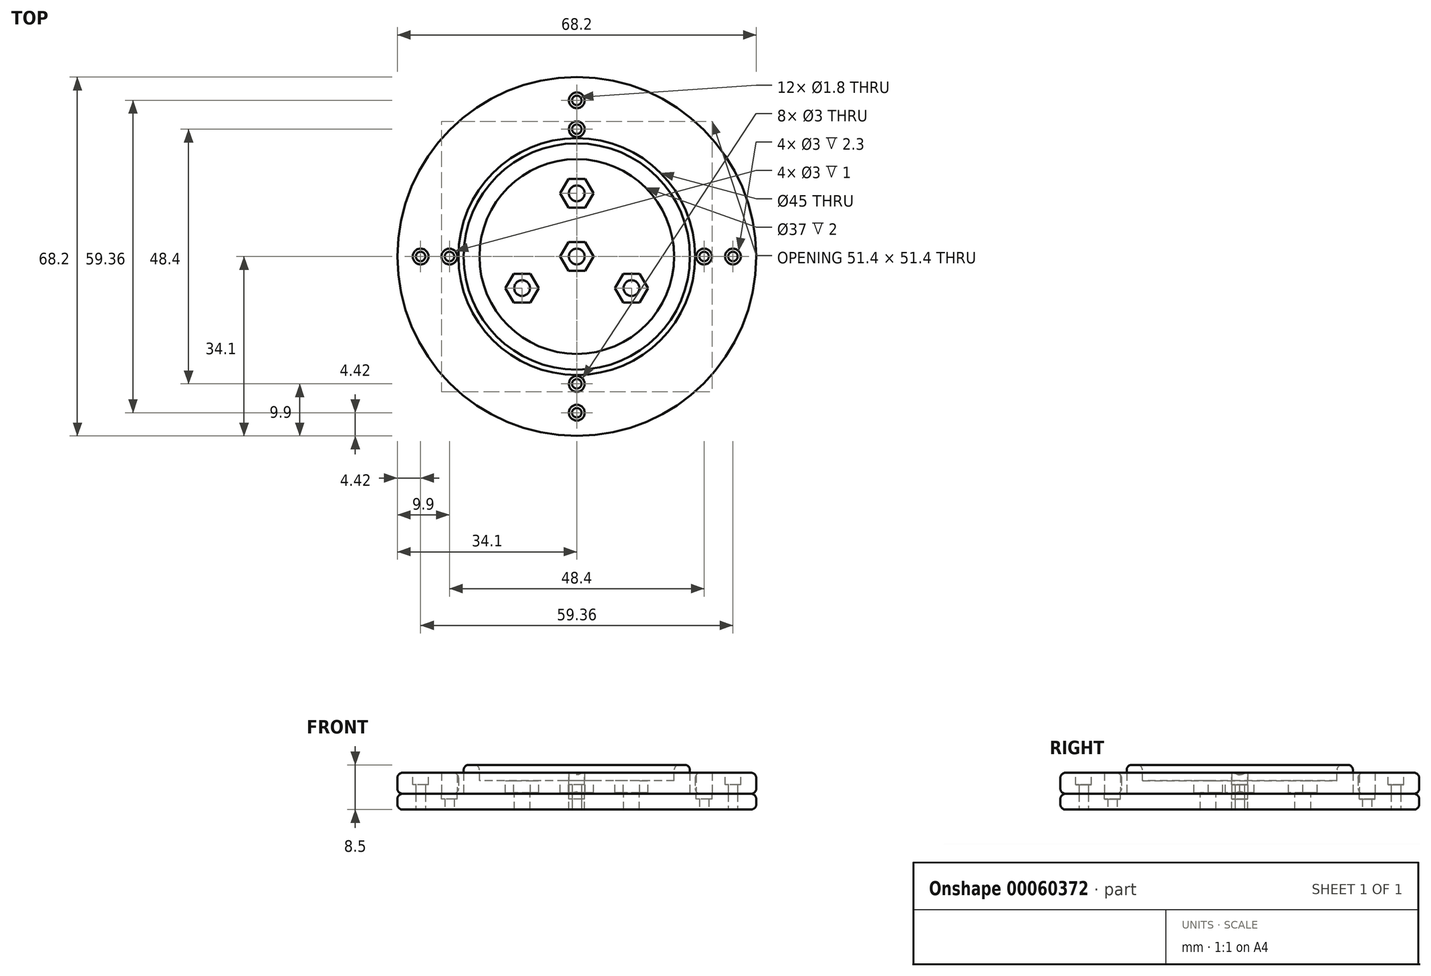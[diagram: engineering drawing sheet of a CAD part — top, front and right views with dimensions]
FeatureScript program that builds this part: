
annotation { "Feature Type Name" : "Feature", "Feature Type Description" : "" }
export const myFeature = defineFeature(function(context is Context, id is Id, definition is map)
    precondition{}
    {
        {
            var Q0;
            Q0=qCreatedBy(makeId("Top.planeOp"),FACE);
            var sketch = newSketch(context, id + "F0", { "sketchPlane" : qUnion([Q0])});
            skCircle(sketch, "E0", {"center": v(0, 0) * mm, "radius": 34.1 * mm});
            skCircle(sketch, "E1", {"center": v(0, 29.68) * mm, "radius": 0.9 * mm});
            skCircle(sketch, "E2", {"center": v(0, 24.2) * mm, "radius": 0.9 * mm});
            skCircle(sketch, "E3.1.0", {"center": v(-29.68, 0) * mm, "radius": 0.9 * mm});
            skCircle(sketch, "E3.1.1", {"center": v(-24.2, 0) * mm, "radius": 0.9 * mm});
            skCircle(sketch, "E3.2.0", {"center": v(0, -29.68) * mm, "radius": 0.9 * mm});
            skCircle(sketch, "E3.2.1", {"center": v(0, -24.2) * mm, "radius": 0.9 * mm});
            skCircle(sketch, "E3.3.0", {"center": v(29.68, 0) * mm, "radius": 0.9 * mm});
            skCircle(sketch, "E3.3.1", {"center": v(24.2, 0) * mm, "radius": 0.9 * mm});
            skSolve(sketch);
        }
        {
            var Q0;
            Q0=makeQuery(id+"F0.imprint","IMPRINT",FACE,{"disambiguationData":[TD([[makeQuery(id+"F0.imprint","IMPRINT",EDGE,{"derivedFrom":sQuery(id+"F0.wireOp",EDGE,"E0")}),1.0]])]});
            extrude(context, id + "F1", {"entities" : qUnion([Q0]), "depth" : 3 * mm});
        }
        {
            var Q0;
            Q0=makeQuery(id+"F1.opExtrude","CAP_FACE",FACE,{"disambiguationData":[OSD([sQuery(id+"F0.wireOp",EDGE,"E0"),sQuery(id+"F0.wireOp",EDGE,"E1"),sQuery(id+"F0.wireOp",EDGE,"E2"),sQuery(id+"F0.wireOp",EDGE,"E3.1.0"),sQuery(id+"F0.wireOp",EDGE,"E3.1.1"),sQuery(id+"F0.wireOp",EDGE,"E3.2.0"),sQuery(id+"F0.wireOp",EDGE,"E3.2.1"),sQuery(id+"F0.wireOp",EDGE,"E3.3.0"),sQuery(id+"F0.wireOp",EDGE,"E3.3.1")])],"isStart":false});
            var sketch = newSketch(context, id + "F2", { "sketchPlane" : qUnion([Q0])});
            skCircle(sketch, "E4", {"center": v(0, 24.2) * mm, "radius": 1.5 * mm});
            skCircle(sketch, "E5.1.0", {"center": v(-24.2, 0) * mm, "radius": 1.5 * mm});
            skCircle(sketch, "E5.2.0", {"center": v(0, -24.2) * mm, "radius": 1.5 * mm});
            skCircle(sketch, "E5.3.0", {"center": v(24.2, 0) * mm, "radius": 1.5 * mm});
            skPoint(sketch, "E5.center", {"position": v(0, 0) * mm});
            skSolve(sketch);
        }
        {
            var Q0;
            Q0 = qSketchRegion(id + "F2", true);
            extrude(context, id + "F3", {"entities" : qUnion([Q0]), "operationType" : NewBodyOperationType.REMOVE, "oppositeDirection" : true, "depth" : 1 * mm});
        }
        {
            var Q0;
            Q0=makeQuery(id+"F1.opExtrude","CAP_FACE",FACE,{"disambiguationData":[OSD([sQuery(id+"F0.wireOp",EDGE,"E0"),sQuery(id+"F0.wireOp",EDGE,"E1"),sQuery(id+"F0.wireOp",EDGE,"E2"),sQuery(id+"F0.wireOp",EDGE,"E3.1.0"),sQuery(id+"F0.wireOp",EDGE,"E3.1.1"),sQuery(id+"F0.wireOp",EDGE,"E3.2.0"),sQuery(id+"F0.wireOp",EDGE,"E3.2.1"),sQuery(id+"F0.wireOp",EDGE,"E3.3.0"),sQuery(id+"F0.wireOp",EDGE,"E3.3.1")])],"isStart":false});
            var sketch = newSketch(context, id + "F4", { "sketchPlane" : qUnion([Q0])});
            skCircle(sketch, "E6", {"center": v(0, 0) * mm, "radius": 21.5 * mm});
            skSolve(sketch);
        }
        {
            var Q0;
            Q0 = qSketchRegion(id + "F4", true);
            extrude(context, id + "F5", {"entities" : qUnion([Q0]), "operationType" : NewBodyOperationType.ADD, "depth" : 5.5 * mm});
        }
        {
            var Q0;
            Q0=makeQuery(id+"F5.opExtrude","CAP_FACE",FACE,{"disambiguationData":[OSD([sQuery(id+"F4.wireOp",EDGE,"E6")])],"isStart":false});
            var sketch = newSketch(context, id + "F6", { "sketchPlane" : qUnion([Q0])});
            skCircle(sketch, "E7", {"center": v(0, 0) * mm, "radius": 18.5 * mm});
            skSolve(sketch);
        }
        {
            var Q0;
            Q0 = qSketchRegion(id + "F6", true);
            extrude(context, id + "F7", {"entities" : qUnion([Q0]), "operationType" : NewBodyOperationType.REMOVE, "oppositeDirection" : true, "depth" : 3 * mm});
        }
        {
            var Q0;
            Q0=makeQuery(id+"F7.boolean.opBoolean","COPY",FACE,{"derivedFrom":makeQuery(id+"F7.opExtrude","CAP_FACE",FACE,{"disambiguationData":[OSD([sQuery(id+"F6.wireOp",EDGE,"E7")])],"isStart":false})});
            var sketch = newSketch(context, id + "F8", { "sketchPlane" : qUnion([Q0])});
            skCircle(sketch, "E8.cCircle", {"center": v(0, 12) * mm, "radius": 2.73 * mm, "construction": true});
            skLineSegment(sketch, "E8.0", {"start": v(1.58, 9.26) * mm, "end": v(-1.58, 9.26) * mm});
            skLineSegment(sketch, "E8.1", {"start": v(-1.58, 9.26) * mm, "end": v(-3.16, 12) * mm});
            skLineSegment(sketch, "E8.2", {"start": v(-3.16, 12) * mm, "end": v(-1.58, 14.73) * mm});
            skLineSegment(sketch, "E8.3", {"start": v(-1.58, 14.73) * mm, "end": v(1.58, 14.73) * mm});
            skLineSegment(sketch, "E8.4", {"start": v(1.58, 14.73) * mm, "end": v(3.16, 12) * mm});
            skLineSegment(sketch, "E8.5", {"start": v(3.16, 12) * mm, "end": v(1.58, 9.26) * mm});
            skPoint(sketch, "E8.0.midPoint", {"position": v(0, 9.27) * mm});
            skCircle(sketch, "E9", {"center": v(0, 12) * mm, "radius": 1.5 * mm});
            skPoint(sketch, "E10.1.0", {"position": v(-8.02, -4.63) * mm});
            skCircle(sketch, "E10.1.1", {"center": v(-10.4, -6) * mm, "radius": 1.5 * mm});
            skLineSegment(sketch, "E10.1.2", {"start": v(-11.97, -3.26) * mm, "end": v(-8.81, -3.26) * mm});
            skLineSegment(sketch, "E10.1.3", {"start": v(-13.55, -6) * mm, "end": v(-11.97, -3.26) * mm});
            skLineSegment(sketch, "E10.1.4", {"start": v(-11.97, -8.73) * mm, "end": v(-13.55, -6) * mm});
            skLineSegment(sketch, "E10.1.5", {"start": v(-8.81, -8.73) * mm, "end": v(-11.97, -8.73) * mm});
            skLineSegment(sketch, "E10.1.6", {"start": v(-7.23, -6) * mm, "end": v(-8.81, -8.73) * mm});
            skCircle(sketch, "E10.1.7", {"center": v(-10.4, -6) * mm, "radius": 2.73 * mm, "construction": true});
            skLineSegment(sketch, "E10.1.8", {"start": v(-8.81, -3.26) * mm, "end": v(-7.23, -6) * mm});
            skPoint(sketch, "E10.2.0", {"position": v(8.02, -4.63) * mm});
            skCircle(sketch, "E10.2.1", {"center": v(10.4, -6) * mm, "radius": 1.5 * mm});
            skLineSegment(sketch, "E10.2.2", {"start": v(8.81, -8.74) * mm, "end": v(7.23, -6) * mm});
            skLineSegment(sketch, "E10.2.3", {"start": v(11.97, -8.73) * mm, "end": v(8.81, -8.73) * mm});
            skLineSegment(sketch, "E10.2.4", {"start": v(13.55, -6) * mm, "end": v(11.97, -8.73) * mm});
            skLineSegment(sketch, "E10.2.5", {"start": v(11.97, -3.26) * mm, "end": v(13.55, -6) * mm});
            skLineSegment(sketch, "E10.2.6", {"start": v(8.81, -3.26) * mm, "end": v(11.97, -3.26) * mm});
            skCircle(sketch, "E10.2.7", {"center": v(10.4, -6) * mm, "radius": 2.73 * mm, "construction": true});
            skLineSegment(sketch, "E10.2.8", {"start": v(7.23, -6) * mm, "end": v(8.81, -3.26) * mm});
            skPoint(sketch, "E10.center", {"position": v(0, 0) * mm});
            skCircle(sketch, "E11", {"center": v(0, 0) * mm, "radius": 1.5 * mm});
            skCircle(sketch, "E12.cCircle", {"center": v(0, 0) * mm, "radius": 2.73 * mm, "construction": true});
            skLineSegment(sketch, "E12.0", {"start": v(1.58, -2.73) * mm, "end": v(-1.58, -2.73) * mm});
            skLineSegment(sketch, "E12.1", {"start": v(-1.58, -2.73) * mm, "end": v(-3.16, 0) * mm});
            skLineSegment(sketch, "E12.2", {"start": v(-3.16, 0) * mm, "end": v(-1.58, 2.73) * mm});
            skLineSegment(sketch, "E12.3", {"start": v(-1.58, 2.73) * mm, "end": v(1.58, 2.74) * mm});
            skLineSegment(sketch, "E12.4", {"start": v(1.58, 2.74) * mm, "end": v(3.16, 0) * mm});
            skLineSegment(sketch, "E12.5", {"start": v(3.16, 0) * mm, "end": v(1.58, -2.73) * mm});
            skPoint(sketch, "E12.0.midPoint", {"position": v(0, -2.73) * mm});
            skSolve(sketch);
        }
        {
            var Q0;
            Q0 = qSketchRegion(id + "F8", true);
            extrude(context, id + "F9", {"entities" : qUnion([Q0]), "operationType" : NewBodyOperationType.REMOVE, "oppositeDirection" : true, "depth" : 2.3 * mm});
        }
        {
            var Q0;
            Q0=makeQuery(id+"F9.boolean.opBoolean","SPLIT",FACE,{"disambiguationData":[TD([makeQuery(id+"F9.opExtrude","SWEPT_FACE",FACE,{"disambiguationData":[OSD([sQuery(id+"F8.wireOp",EDGE,"E9")])]})])],"derivedFrom":makeQuery(id+"F7.boolean.opBoolean","COPY",FACE,{"derivedFrom":makeQuery(id+"F7.opExtrude","CAP_FACE",FACE,{"disambiguationData":[OSD([sQuery(id+"F6.wireOp",EDGE,"E7")])],"isStart":false})})});
            var Q1;
            Q1=makeQuery(id+"F9.boolean.opBoolean","SPLIT",FACE,{"disambiguationData":[TD([makeQuery(id+"F9.opExtrude","SWEPT_FACE",FACE,{"disambiguationData":[OSD([sQuery(id+"F8.wireOp",EDGE,"E10.2.1")])]})])],"derivedFrom":makeQuery(id+"F7.boolean.opBoolean","COPY",FACE,{"derivedFrom":makeQuery(id+"F7.opExtrude","CAP_FACE",FACE,{"disambiguationData":[OSD([sQuery(id+"F6.wireOp",EDGE,"E7")])],"isStart":false})})});
            var Q2;
            Q2=makeQuery(id+"F9.boolean.opBoolean","SPLIT",FACE,{"disambiguationData":[TD([makeQuery(id+"F9.opExtrude","SWEPT_FACE",FACE,{"disambiguationData":[OSD([sQuery(id+"F8.wireOp",EDGE,"E10.1.1")])]})])],"derivedFrom":makeQuery(id+"F7.boolean.opBoolean","COPY",FACE,{"derivedFrom":makeQuery(id+"F7.opExtrude","CAP_FACE",FACE,{"disambiguationData":[OSD([sQuery(id+"F6.wireOp",EDGE,"E7")])],"isStart":false})})});
            var Q3;
            Q3=makeQuery(id+"F9.boolean.opBoolean","SPLIT",FACE,{"disambiguationData":[TD([makeQuery(id+"F9.opExtrude","SWEPT_FACE",FACE,{"disambiguationData":[OSD([sQuery(id+"F8.wireOp",EDGE,"E11")])]})])],"derivedFrom":makeQuery(id+"F7.boolean.opBoolean","COPY",FACE,{"derivedFrom":makeQuery(id+"F7.opExtrude","CAP_FACE",FACE,{"disambiguationData":[OSD([sQuery(id+"F6.wireOp",EDGE,"E7")])],"isStart":false})})});
            var Q4;
            Q4=makeQuery(id+"F9.boolean.opBoolean","SPLIT",FACE,{"disambiguationData":[TD([makeQuery(id+"F9.opExtrude","SWEPT_FACE",FACE,{"disambiguationData":[OSD([sQuery(id+"F8.wireOp",EDGE,"E11")])]})])],"derivedFrom":makeQuery(id+"F7.boolean.opBoolean","COPY",FACE,{"derivedFrom":makeQuery(id+"F7.opExtrude","CAP_FACE",FACE,{"disambiguationData":[OSD([sQuery(id+"F6.wireOp",EDGE,"E7")])],"isStart":false})})});
            var Q5;
            Q5=makeQuery(id+"F9.boolean.opBoolean","SPLIT",FACE,{"disambiguationData":[TD([makeQuery(id+"F9.opExtrude","SWEPT_FACE",FACE,{"disambiguationData":[OSD([sQuery(id+"F8.wireOp",EDGE,"E11")])]})])],"derivedFrom":makeQuery(id+"F7.boolean.opBoolean","COPY",FACE,{"derivedFrom":makeQuery(id+"F7.opExtrude","CAP_FACE",FACE,{"disambiguationData":[OSD([sQuery(id+"F6.wireOp",EDGE,"E7")])],"isStart":false})})});
            var Q6;
            Q6=makeQuery(id+"F9.boolean.opBoolean","SPLIT",FACE,{"disambiguationData":[TD([makeQuery(id+"F9.opExtrude","SWEPT_FACE",FACE,{"disambiguationData":[OSD([sQuery(id+"F8.wireOp",EDGE,"E11")])]})])],"derivedFrom":makeQuery(id+"F7.boolean.opBoolean","COPY",FACE,{"derivedFrom":makeQuery(id+"F7.opExtrude","CAP_FACE",FACE,{"disambiguationData":[OSD([sQuery(id+"F6.wireOp",EDGE,"E7")])],"isStart":false})})});
            extrude(context, id + "F10", {"entities" : qUnion([Q0, Q1, Q2, Q3, Q4, Q5, Q6]), "operationType" : NewBodyOperationType.REMOVE, "endBound" : BoundingType.THROUGH_ALL, "oppositeDirection" : true, "depth" : 25 * mm});
        }
        {
            var Q0;
            Q0=makeQuery(id+"F1.opExtrude","CAP_FACE",FACE,{"disambiguationData":[OSD([sQuery(id+"F0.wireOp",EDGE,"E0"),sQuery(id+"F0.wireOp",EDGE,"E1"),sQuery(id+"F0.wireOp",EDGE,"E2"),sQuery(id+"F0.wireOp",EDGE,"E3.1.0"),sQuery(id+"F0.wireOp",EDGE,"E3.1.1"),sQuery(id+"F0.wireOp",EDGE,"E3.2.0"),sQuery(id+"F0.wireOp",EDGE,"E3.2.1"),sQuery(id+"F0.wireOp",EDGE,"E3.3.0"),sQuery(id+"F0.wireOp",EDGE,"E3.3.1")])],"isStart":false});
            var sketch = newSketch(context, id + "F11", { "sketchPlane" : qUnion([Q0])});
            skCircle(sketch, "E13", {"center": v(0, 0) * mm, "radius": 22.5 * mm});
            skCircle(sketch, "E14", {"center": v(0, 0) * mm, "radius": 34.1 * mm});
            skCircle(sketch, "E15", {"center": v(0, 29.68) * mm, "radius": 1.5 * mm});
            skCircle(sketch, "E16.1.0", {"center": v(-29.68, 0) * mm, "radius": 1.5 * mm});
            skCircle(sketch, "E16.2.0", {"center": v(0, -29.68) * mm, "radius": 1.5 * mm});
            skCircle(sketch, "E16.3.0", {"center": v(29.68, 0) * mm, "radius": 1.5 * mm});
            skSolve(sketch);
        }
        {
            var Q0;
            Q0=makeQuery(id+"F11.imprint","IMPRINT",FACE,{"disambiguationData":[TD([[makeQuery(id+"F11.imprint","IMPRINT",EDGE,{"derivedFrom":sQuery(id+"F11.wireOp",EDGE,"E13")}),-1.0]])]});
            var Q1;
            Q1=makeQuery(id+"F11.imprint","IMPRINT",FACE,{"disambiguationData":[TD([[makeQuery(id+"F11.imprint","IMPRINT",EDGE,{"derivedFrom":makeQuery(id+"F3.boolean.opBoolean","COPY",EDGE,{"derivedFrom":makeQuery(id+"F3.opExtrude","CAP_EDGE",EDGE,{"disambiguationData":[OSD([sQuery(id+"F2.wireOp",EDGE,"E5.1.0")])],"isStart":true})})}),1.0]])]});
            var Q2;
            Q2=makeQuery(id+"F11.imprint","IMPRINT",FACE,{"disambiguationData":[TD([[makeQuery(id+"F11.imprint","IMPRINT",EDGE,{"derivedFrom":makeQuery(id+"F3.boolean.opBoolean","COPY",EDGE,{"derivedFrom":makeQuery(id+"F3.opExtrude","CAP_EDGE",EDGE,{"disambiguationData":[OSD([sQuery(id+"F2.wireOp",EDGE,"E4")])],"isStart":true})})}),1.0]])]});
            var Q3;
            Q3=makeQuery(id+"F11.imprint","IMPRINT",FACE,{"disambiguationData":[TD([[makeQuery(id+"F11.imprint","IMPRINT",EDGE,{"derivedFrom":makeQuery(id+"F3.boolean.opBoolean","COPY",EDGE,{"derivedFrom":makeQuery(id+"F3.opExtrude","CAP_EDGE",EDGE,{"disambiguationData":[OSD([sQuery(id+"F2.wireOp",EDGE,"E5.3.0")])],"isStart":true})})}),1.0]])]});
            var Q4;
            Q4=makeQuery(id+"F11.imprint","IMPRINT",FACE,{"disambiguationData":[TD([[makeQuery(id+"F11.imprint","IMPRINT",EDGE,{"derivedFrom":makeQuery(id+"F3.boolean.opBoolean","COPY",EDGE,{"derivedFrom":makeQuery(id+"F3.opExtrude","CAP_EDGE",EDGE,{"disambiguationData":[OSD([sQuery(id+"F2.wireOp",EDGE,"E5.2.0")])],"isStart":true})})}),1.0]])]});
            var Q5;
            Q5=makeQuery(id+"F11.imprint","IMPRINT",FACE,{"disambiguationData":[TD([[makeQuery(id+"F11.imprint","IMPRINT",EDGE,{"derivedFrom":sQuery(id+"F11.wireOp",EDGE,"E15")}),1.0]])]});
            var Q6;
            Q6=makeQuery(id+"F11.imprint","IMPRINT",FACE,{"disambiguationData":[TD([[makeQuery(id+"F11.imprint","IMPRINT",EDGE,{"derivedFrom":sQuery(id+"F11.wireOp",EDGE,"E16.1.0")}),1.0]])]});
            var Q7;
            Q7=makeQuery(id+"F11.imprint","IMPRINT",FACE,{"disambiguationData":[TD([[makeQuery(id+"F11.imprint","IMPRINT",EDGE,{"derivedFrom":sQuery(id+"F11.wireOp",EDGE,"E16.2.0")}),1.0]])]});
            var Q8;
            Q8=makeQuery(id+"F11.imprint","IMPRINT",FACE,{"disambiguationData":[TD([[makeQuery(id+"F11.imprint","IMPRINT",EDGE,{"derivedFrom":sQuery(id+"F11.wireOp",EDGE,"E16.3.0")}),1.0]])]});
            extrude(context, id + "F12", {"entities" : qUnion([Q0, Q1, Q2, Q3, Q4, Q5, Q6, Q7, Q8]), "depth" : 4 * mm});
        }
        {
            var Q0;
            Q0=makeQuery(id+"F12.opExtrude","CAP_FACE",FACE,{"disambiguationData":[OSD([sQuery(id+"F0.wireOp",EDGE,"E1"),sQuery(id+"F0.wireOp",EDGE,"E3.1.0"),sQuery(id+"F0.wireOp",EDGE,"E3.2.0"),sQuery(id+"F0.wireOp",EDGE,"E3.3.0"),sQuery(id+"F11.wireOp",EDGE,"E13"),sQuery(id+"F11.wireOp",EDGE,"E14")])],"isStart":false});
            var sketch = newSketch(context, id + "F13", { "sketchPlane" : qUnion([Q0])});
            skCircle(sketch, "E17", {"center": v(0, 29.68) * mm, "radius": 1.5 * mm});
            skCircle(sketch, "E18.1.0", {"center": v(-29.68, 0) * mm, "radius": 1.5 * mm});
            skCircle(sketch, "E18.2.0", {"center": v(0, -29.68) * mm, "radius": 1.5 * mm});
            skCircle(sketch, "E18.3.0", {"center": v(29.68, 0) * mm, "radius": 1.5 * mm});
            skPoint(sketch, "E18.center", {"position": v(0, 0) * mm});
            skSolve(sketch);
        }
        {
            var Q0;
            Q0 = qSketchRegion(id + "F13", true);
            extrude(context, id + "F14", {"entities" : qUnion([Q0]), "operationType" : NewBodyOperationType.REMOVE, "oppositeDirection" : true, "depth" : 2.3 * mm});
        }
        {
            var Q0;
            Q0=makeQuery(id+"F5.opExtrude","CAP_FACE",FACE,{"disambiguationData":[OSD([sQuery(id+"F4.wireOp",EDGE,"E6")])],"isStart":false});
            fillet(context, id + "F15", {"entities" : qUnion([Q0]), "radius" : 1 * mm, "tangentPropagation" : true, "allowEdgeOverflow" : false});
        }
        {
            var Q0;
            Q0=makeQuery(id+"F12.opExtrude","CAP_EDGE",EDGE,{"disambiguationData":[OSD([sQuery(id+"F11.wireOp",EDGE,"E13")])],"isStart":true});
            var Q1;
            Q1=makeQuery(id+"F12.opExtrude","CAP_EDGE",EDGE,{"disambiguationData":[OSD([sQuery(id+"F11.wireOp",EDGE,"E13")])],"isStart":false});
            var Q2;
            Q2=makeQuery(id+"F12.opExtrude","CAP_EDGE",EDGE,{"disambiguationData":[OSD([sQuery(id+"F11.wireOp",EDGE,"E14")])],"isStart":false});
            var Q3;
            Q3=makeQuery(id+"F12.opExtrude","CAP_EDGE",EDGE,{"disambiguationData":[OSD([sQuery(id+"F11.wireOp",EDGE,"E14")])],"isStart":true});
            fillet(context, id + "F16", {"entities" : qUnion([Q0, Q1, Q2, Q3]), "radius" : 1 * mm, "tangentPropagation" : true, "allowEdgeOverflow" : false});
        }
        {
            var Q0;
            Q0=makeQuery(id+"F1.opExtrude","CAP_EDGE",EDGE,{"disambiguationData":[OSD([sQuery(id+"F0.wireOp",EDGE,"E0")])],"isStart":false});
            var Q1;
            Q1=makeQuery(id+"F1.opExtrude","CAP_EDGE",EDGE,{"disambiguationData":[OSD([sQuery(id+"F0.wireOp",EDGE,"E0")])],"isStart":true});
            var Q2;
            Q2=makeQuery(id+"F5.opExtrude","CAP_EDGE",EDGE,{"disambiguationData":[OSD([sQuery(id+"F4.wireOp",EDGE,"E6")])],"isStart":true});
            fillet(context, id + "F17", {"entities" : qUnion([Q0, Q1, Q2]), "radius" : 1 * mm, "tangentPropagation" : true, "allowEdgeOverflow" : false});
        }
    });
